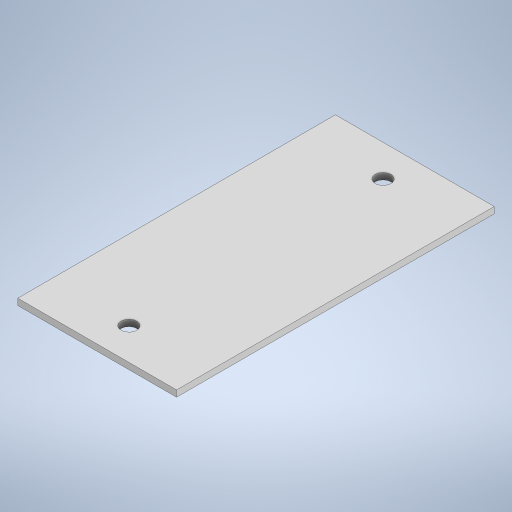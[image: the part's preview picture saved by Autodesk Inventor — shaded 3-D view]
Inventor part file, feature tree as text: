
AUTODESK INVENTOR PART (.ipt)
format: ipt  version: 2023 (Build 270158000, 158)  size: 215,040 bytes
history: native  units: mm
features: extrude x1, sketch x1
ambient origin geometry x8: Origin, YZ Plane, XZ Plane, XY Plane, X Axis, Y Axis, Z Axis, Center Point
bodies: Solid1 (feature_tree)
feature tree (2):
  extrude  "Extrusion1"  Depth=100.0mm
  sketch  "Sketch1"  dims[d0=50.0mm d1=100.0mm d2=10.0mm d3=10.0mm d4=5.0mm d5=5.0mm d6=2.0mm d7=0.0mm]
